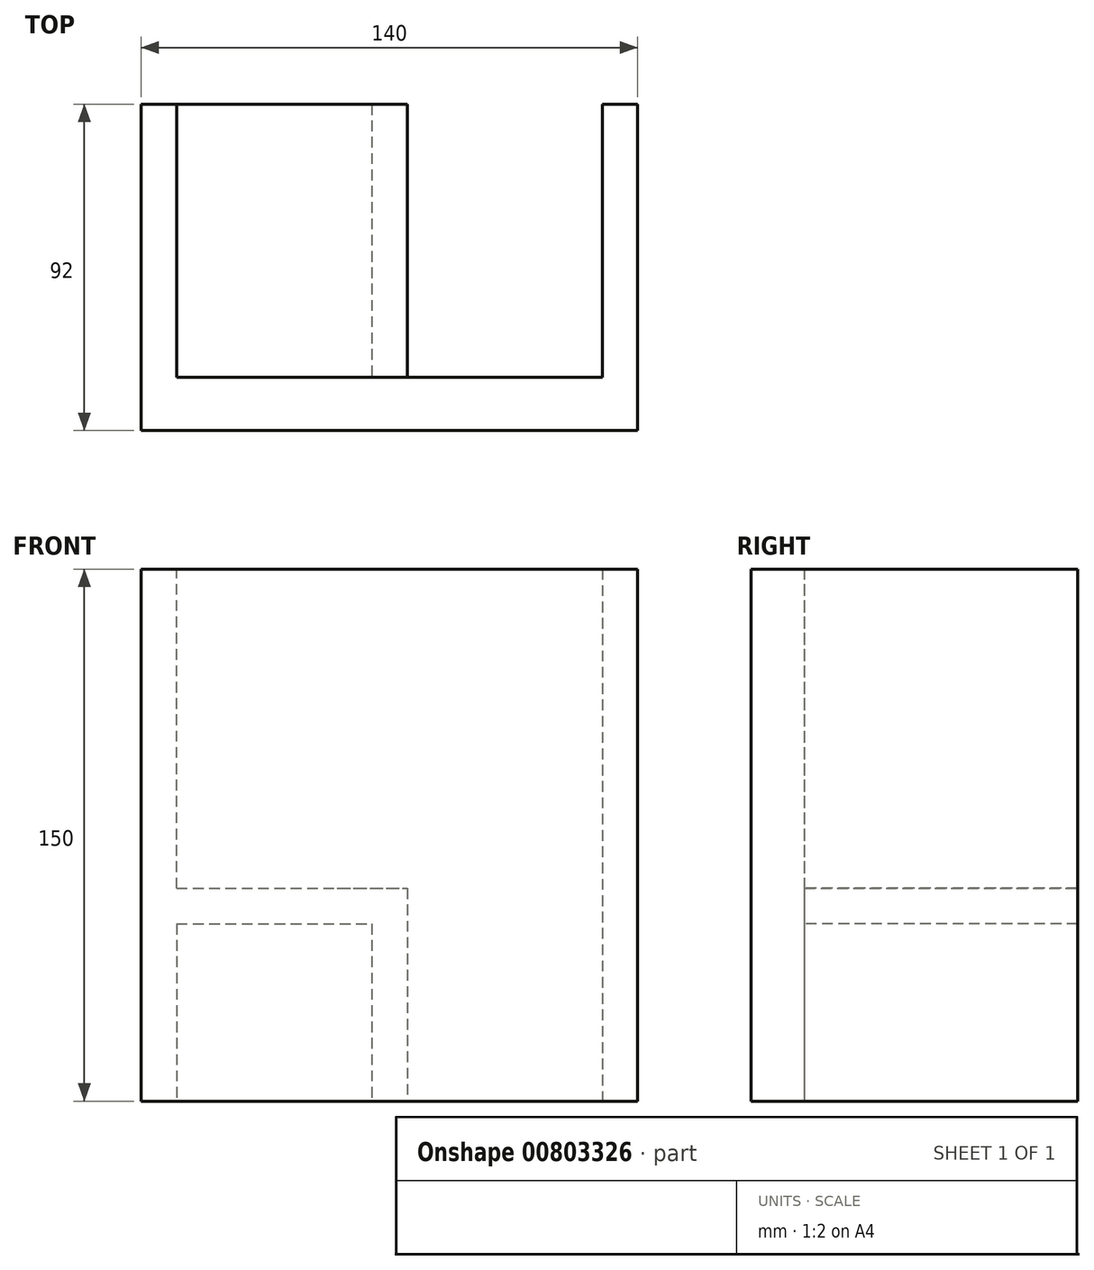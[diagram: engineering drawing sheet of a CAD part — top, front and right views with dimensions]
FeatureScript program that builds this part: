
annotation { "Feature Type Name" : "Feature", "Feature Type Description" : "" }
export const myFeature = defineFeature(function(context is Context, id is Id, definition is map)
    precondition{}
    {
        {
            var Q0;
            Q0=qCreatedBy(makeId("Top.planeOp"),FACE);
            var sketch = newSketch(context, id + "F0", { "sketchPlane" : qUnion([Q0])});
            skLineSegment(sketch, "E0", {"start": v(-46.42, 59.16) * mm, "end": v(-46.42, -32.84) * mm});
            skLineSegment(sketch, "E1", {"start": v(-46.42, -32.84) * mm, "end": v(93.58, -32.84) * mm});
            skLineSegment(sketch, "E2", {"start": v(93.58, -32.84) * mm, "end": v(93.58, 59.16) * mm});
            skLineSegment(sketch, "E3", {"start": v(93.58, 59.16) * mm, "end": v(83.58, 59.16) * mm});
            skLineSegment(sketch, "E4", {"start": v(83.58, 59.16) * mm, "end": v(83.58, -17.84) * mm});
            skLineSegment(sketch, "E5", {"start": v(83.58, -17.84) * mm, "end": v(28.58, -17.84) * mm});
            skLineSegment(sketch, "E6", {"start": v(28.58, -17.84) * mm, "end": v(28.58, 59.16) * mm});
            skLineSegment(sketch, "E7", {"start": v(28.58, 59.16) * mm, "end": v(18.58, 59.16) * mm});
            skLineSegment(sketch, "E8", {"start": v(18.58, 59.16) * mm, "end": v(18.58, -17.84) * mm});
            skLineSegment(sketch, "E9", {"start": v(18.58, -17.84) * mm, "end": v(-36.42, -17.84) * mm});
            skLineSegment(sketch, "E10", {"start": v(-36.42, -17.84) * mm, "end": v(-36.42, 59.16) * mm});
            skLineSegment(sketch, "E11", {"start": v(-36.42, 59.16) * mm, "end": v(-46.42, 59.16) * mm});
            skSolve(sketch);
        }
        {
            var Q0;
            Q0=makeQuery(id+"F0.imprint","IMPRINT",FACE,{"disambiguationData":[TD([[makeQuery(id+"F0.imprint","IMPRINT",EDGE,{"derivedFrom":sQuery(id+"F0.wireOp",EDGE,"E0")}),1.0]])]});
            extrude(context, id + "F1", {"entities" : qUnion([Q0]), "depth" : 50 * mm, "offsetDistance" : 25 * mm});
        }
        {
            var Q0;
            Q0=makeQuery(id+"F1.opExtrude","CAP_FACE",FACE,{"disambiguationData":[OSD([sQuery(id+"F0.wireOp",EDGE,"E0"),sQuery(id+"F0.wireOp",EDGE,"E1"),sQuery(id+"F0.wireOp",EDGE,"E2"),sQuery(id+"F0.wireOp",EDGE,"E3"),sQuery(id+"F0.wireOp",EDGE,"E4"),sQuery(id+"F0.wireOp",EDGE,"E5"),sQuery(id+"F0.wireOp",EDGE,"E6"),sQuery(id+"F0.wireOp",EDGE,"E7"),sQuery(id+"F0.wireOp",EDGE,"E8"),sQuery(id+"F0.wireOp",EDGE,"E9"),sQuery(id+"F0.wireOp",EDGE,"E10"),sQuery(id+"F0.wireOp",EDGE,"E11")])],"isStart":false});
            var sketch = newSketch(context, id + "F2", { "sketchPlane" : qUnion([Q0])});
            skLineSegment(sketch, "E12", {"start": v(-36.42, 59.16) * mm, "end": v(18.58, 59.16) * mm});
            skSolve(sketch);
        }
        {
            var Q0;
            Q0=makeQuery(id+"F2.imprint","IMPRINT",FACE,{"disambiguationData":[TD([[makeQuery(id+"F2.imprint","IMPRINT",EDGE,{"derivedFrom":sQuery(id+"F2.wireOp",EDGE,"E12")}),-1.0]])]});
            var Q1;
            Q1=makeQuery(id+"F2.imprint","IMPRINT",FACE,{"disambiguationData":[TD([[makeQuery(id+"F2.imprint","IMPRINT",EDGE,{"derivedFrom":makeQuery(id+"F1.opExtrude","CAP_EDGE",EDGE,{"disambiguationData":[OSD([sQuery(id+"F0.wireOp",EDGE,"E0")])],"isStart":false})}),1.0]])]});
            extrude(context, id + "F3", {"entities" : qUnion([Q0, Q1]), "operationType" : NewBodyOperationType.ADD, "depth" : 100 * mm, "offsetDistance" : 25 * mm});
        }
        {
            var Q0;
            Q0=makeQuery(id+"F3.opExtrude","CAP_FACE",FACE,{"disambiguationData":[OSD([sQuery(id+"F0.wireOp",EDGE,"E0"),sQuery(id+"F0.wireOp",EDGE,"E1"),sQuery(id+"F0.wireOp",EDGE,"E2"),sQuery(id+"F0.wireOp",EDGE,"E3"),sQuery(id+"F0.wireOp",EDGE,"E4"),sQuery(id+"F0.wireOp",EDGE,"E5"),sQuery(id+"F0.wireOp",EDGE,"E6"),sQuery(id+"F0.wireOp",EDGE,"E7"),sQuery(id+"F0.wireOp",EDGE,"E11"),sQuery(id+"F2.wireOp",EDGE,"E12")])],"isStart":false});
            var sketch = newSketch(context, id + "F4", { "sketchPlane" : qUnion([Q0])});
            skLineSegment(sketch, "E13", {"start": v(-36.42, 59.16) * mm, "end": v(-36.42, -17.76) * mm});
            skLineSegment(sketch, "E14", {"start": v(-36.42, -17.76) * mm, "end": v(8.86, -17.76) * mm});
            skLineSegment(sketch, "E15", {"start": v(8.86, -17.76) * mm, "end": v(28.58, -17.84) * mm});
            skLineSegment(sketch, "E16", {"start": v(28.58, -17.84) * mm, "end": v(28.58, 59.16) * mm});
            skLineSegment(sketch, "E17", {"start": v(28.58, 59.16) * mm, "end": v(-36.42, 59.16) * mm});
            skSolve(sketch);
        }
        {
            var Q0;
            Q0=makeQuery(id+"F4.imprint","IMPRINT",FACE,{"disambiguationData":[TD([[makeQuery(id+"F4.imprint","IMPRINT",EDGE,{"derivedFrom":sQuery(id+"F4.wireOp",EDGE,"E13")}),1.0]])]});
            extrude(context, id + "F5", {"entities" : qUnion([Q0]), "operationType" : NewBodyOperationType.REMOVE, "oppositeDirection" : true, "depth" : 90 * mm, "offsetDistance" : 25 * mm});
        }
    });
